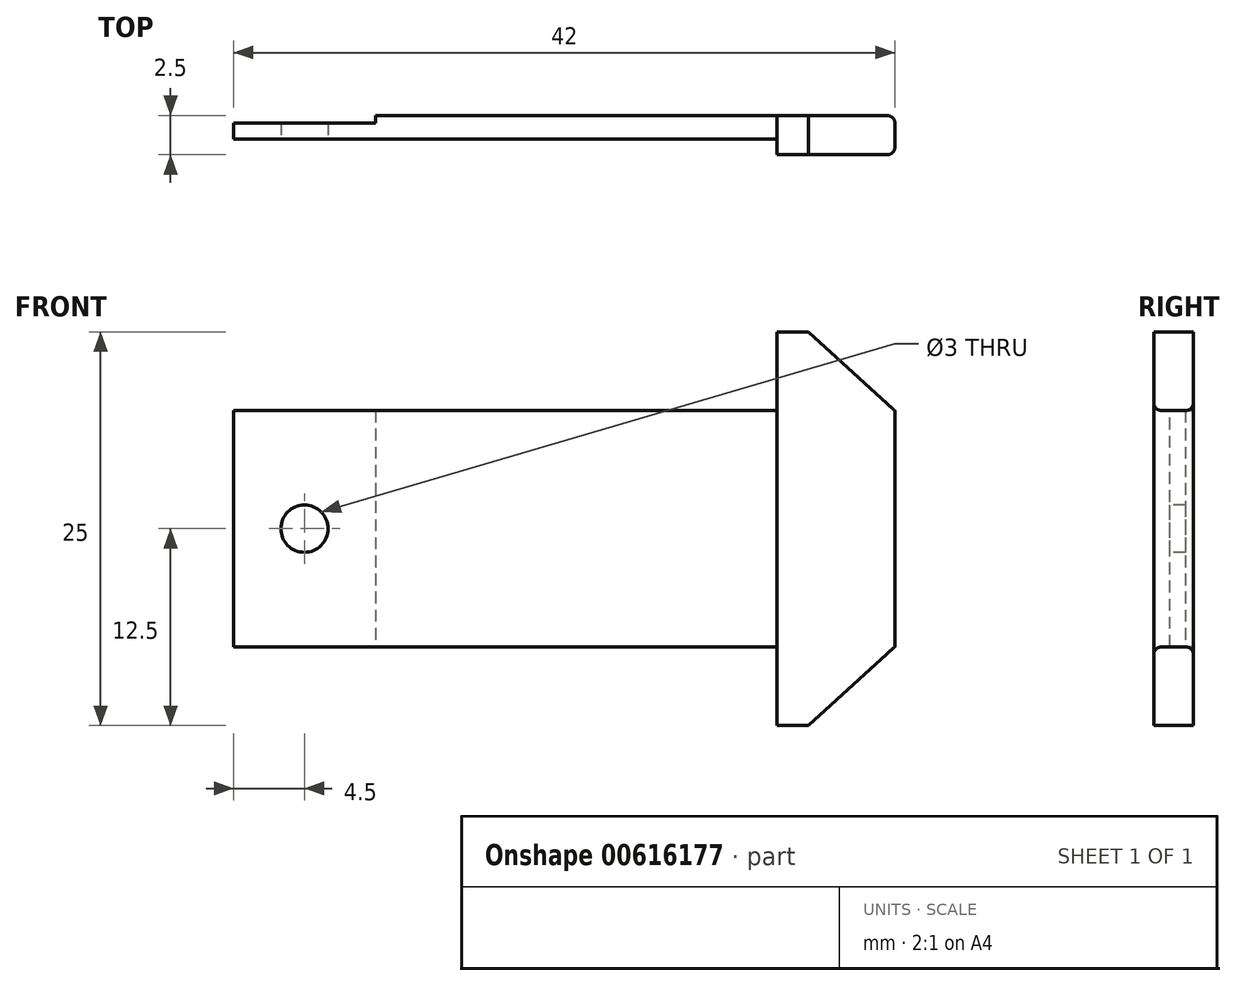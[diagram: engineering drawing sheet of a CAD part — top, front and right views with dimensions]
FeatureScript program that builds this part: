
annotation { "Feature Type Name" : "Feature", "Feature Type Description" : "" }
export const myFeature = defineFeature(function(context is Context, id is Id, definition is map)
    precondition{}
    {
        {
            var Q0;
            Q0=qCreatedBy(makeId("Front.planeOp"),FACE);
            var sketch = newSketch(context, id + "F0", { "sketchPlane" : qUnion([Q0])});
            skLineSegment(sketch, "E0.bottom", {"start": v(-17, 7.5) * mm, "end": v(25, 7.5) * mm});
            skLineSegment(sketch, "E0.top", {"start": v(-17, -7.5) * mm, "end": v(25, -7.5) * mm});
            skLineSegment(sketch, "E0.left", {"start": v(-17, 7.5) * mm, "end": v(-17, -7.5) * mm});
            skLineSegment(sketch, "E0.right", {"start": v(25, 7.5) * mm, "end": v(25, -7.5) * mm});
            skPoint(sketch, "E0.middle", {"position": v(4, 0) * mm});
            skSolve(sketch);
        }
        {
            var Q0;
            Q0=qSketchRegion(id+"F0",true);
            extrude(context, id + "F1", {"entities" : qUnion([Q0]), "depth" : 1.5 * mm, "offsetDistance" : 25 * mm});
        }
        {
            var Q0;
            Q0=makeQuery(id+"Fg7a1GXraSj58Eq_1.boolean.opBoolean","MERGE",FACE,{"derivedFrom":[makeQuery(id+"F1.opExtrude","CAP_FACE",FACE,{"disambiguationData":[OSD([sQuery(id+"F0.wireOp",EDGE,"E0.bottom"),sQuery(id+"F0.wireOp",EDGE,"E0.top"),sQuery(id+"F0.wireOp",EDGE,"E0.left"),sQuery(id+"F0.wireOp",EDGE,"E0.right")])],"isStart":false}),makeQuery(id+"Fg7a1GXraSj58Eq_1.opExtrude","CAP_FACE",FACE,{"disambiguationData":[OSD([sQuery(id+"F8gBCBH27mQZ7OE_1.wireOp",EDGE,"RbVLayld-Gt7w-auHQ-ZlfH-3jq96yst7m8C.bottom"),sQuery(id+"F8gBCBH27mQZ7OE_1.wireOp",EDGE,"RbVLayld-Gt7w-auHQ-ZlfH-3jq96yst7m8C.top"),sQuery(id+"F8gBCBH27mQZ7OE_1.wireOp",EDGE,"RbVLayld-Gt7w-auHQ-ZlfH-3jq96yst7m8C.left"),sQuery(id+"F8gBCBH27mQZ7OE_1.wireOp",EDGE,"RbVLayld-Gt7w-auHQ-ZlfH-3jq96yst7m8C.right")])],"isStart":true})]});
            var sketch = newSketch(context, id + "F2", { "sketchPlane" : qUnion([Q0])});
            skCircle(sketch, "E1", {"center": v(-12.5, 0) * mm, "radius": 1.5 * mm});
            skPoint(sketch, "E2", {"position": v(-17, 0) * mm});
            skSolve(sketch);
        }
        {
            var Q0;
            Q0 = qSketchRegion(id + "F2", true);
            extrude(context, id + "F3", {"entities" : qUnion([Q0]), "operationType" : NewBodyOperationType.REMOVE, "endBound" : BoundingType.THROUGH_ALL, "oppositeDirection" : true, "depth" : 25 * mm, "offsetDistance" : 25 * mm});
        }
        {
            var Q0;
            Q0=makeQuery(id+"F1.opExtrude","CAP_FACE",FACE,{"disambiguationData":[OSD([sQuery(id+"F0.wireOp",EDGE,"E0.bottom"),sQuery(id+"F0.wireOp",EDGE,"E0.top"),sQuery(id+"F0.wireOp",EDGE,"E0.left"),sQuery(id+"F0.wireOp",EDGE,"E0.right")])],"isStart":false});
            var sketch = newSketch(context, id + "F4", { "sketchPlane" : qUnion([Q0])});
            skLineSegment(sketch, "E3.bottom", {"start": v(25, -7.5) * mm, "end": v(17.5, -7.5) * mm});
            skLineSegment(sketch, "E3.top", {"start": v(19.5, -12.5) * mm, "end": v(17.5, -12.5) * mm});
            skLineSegment(sketch, "E3.right", {"start": v(17.5, -7.5) * mm, "end": v(17.5, -12.5) * mm});
            skLineSegment(sketch, "E4.bottom", {"start": v(25, 7.5) * mm, "end": v(17.5, 7.5) * mm});
            skLineSegment(sketch, "E4.top", {"start": v(19.5, 12.5) * mm, "end": v(17.5, 12.5) * mm});
            skLineSegment(sketch, "E4.right", {"start": v(17.5, 7.5) * mm, "end": v(17.5, 12.5) * mm});
            skLineSegment(sketch, "E5", {"start": v(17.5, -12.5) * mm, "end": v(19.5, -12.5) * mm});
            skLineSegment(sketch, "E6", {"start": v(19.5, -12.5) * mm, "end": v(25, -7.5) * mm});
            skLineSegment(sketch, "E7.MirrorCS", {"start": v(19.5, 12.5) * mm, "end": v(25, 7.5) * mm});
            skLineSegment(sketch, "E8.MirrorCS", {"start": v(17.5, 12.5) * mm, "end": v(19.5, 12.5) * mm});
            skSolve(sketch);
        }
        {
            var Q0;
            Q0 = qSketchRegion(id + "F4", true);
            var Q1;
            Q1=makeQuery(id+"F1.opExtrude","CAP_FACE",FACE,{"disambiguationData":[OSD([sQuery(id+"F0.wireOp",EDGE,"E0.bottom"),sQuery(id+"F0.wireOp",EDGE,"E0.top"),sQuery(id+"F0.wireOp",EDGE,"E0.left"),sQuery(id+"F0.wireOp",EDGE,"E0.right")])],"isStart":true});
            extrude(context, id + "F5", {"entities" : qUnion([Q0]), "operationType" : NewBodyOperationType.ADD, "endBound" : BoundingType.UP_TO_SURFACE, "oppositeDirection" : true, "depth" : 25 * mm, "endBoundEntityFace" : qUnion([Q1]), "offsetDistance" : 25 * mm});
        }
        {
            var Q0;
            Q0=makeQuery(id+"F1.opExtrude","SWEPT_FACE",FACE,{"disambiguationData":[OSD([sQuery(id+"F0.wireOp",EDGE,"E0.top")])]});
            var sketch = newSketch(context, id + "F6", { "sketchPlane" : qUnion([Q0])});
            skLineSegment(sketch, "E9.bottom", {"start": v(-17, 0) * mm, "end": v(-8, 0) * mm});
            skLineSegment(sketch, "E9.top", {"start": v(-17, 0.5) * mm, "end": v(-8, 0.5) * mm});
            skLineSegment(sketch, "E9.left", {"start": v(-17, 0) * mm, "end": v(-17, 0.5) * mm});
            skLineSegment(sketch, "E9.right", {"start": v(-8, 0) * mm, "end": v(-8, 0.5) * mm});
            skSolve(sketch);
        }
        {
            var Q0;
            Q0 = qSketchRegion(id + "F6", true);
            extrude(context, id + "F7", {"entities" : qUnion([Q0]), "operationType" : NewBodyOperationType.REMOVE, "endBound" : BoundingType.THROUGH_ALL, "oppositeDirection" : true, "depth" : 25 * mm, "offsetDistance" : 25 * mm});
        }
        {
            var Q0;
            Q0=makeQuery(id+"F5.boolean.opBoolean","MERGE",FACE,{"derivedFrom":[makeQuery(id+"F1.opExtrude","CAP_FACE",FACE,{"disambiguationData":[OSD([sQuery(id+"F0.wireOp",EDGE,"E0.bottom"),sQuery(id+"F0.wireOp",EDGE,"E0.top"),sQuery(id+"F0.wireOp",EDGE,"E0.left"),sQuery(id+"F0.wireOp",EDGE,"E0.right")])],"isStart":false}),makeQuery(id+"F5.opExtrude","CAP_FACE",FACE,{"disambiguationData":[OSD([sQuery(id+"F4.wireOp",EDGE,"E3.bottom"),sQuery(id+"F4.wireOp",EDGE,"E3.right"),sQuery(id+"F4.wireOp",EDGE,"E5"),sQuery(id+"F4.wireOp",EDGE,"E6")])],"isStart":true}),makeQuery(id+"F5.opExtrude","CAP_FACE",FACE,{"disambiguationData":[OSD([sQuery(id+"F4.wireOp",EDGE,"E4.bottom"),sQuery(id+"F4.wireOp",EDGE,"E4.right"),sQuery(id+"F4.wireOp",EDGE,"E7.MirrorCS"),sQuery(id+"F4.wireOp",EDGE,"E8.MirrorCS")])],"isStart":true})]});
            var sketch = newSketch(context, id + "F8", { "sketchPlane" : qUnion([Q0])});
            skLineSegment(sketch, "E10.0", {"start": v(19.5, 12.5) * mm, "end": v(25, 7.5) * mm});
            skLineSegment(sketch, "E11.0", {"start": v(25, 7.5) * mm, "end": v(25, -7.5) * mm});
            skLineSegment(sketch, "E12.0", {"start": v(19.5, -12.5) * mm, "end": v(25, -7.5) * mm});
            skLineSegment(sketch, "E13", {"start": v(19.5, 12.5) * mm, "end": v(17.5, 12.5) * mm});
            skLineSegment(sketch, "E14", {"start": v(17.5, 12.5) * mm, "end": v(17.5, -12.5) * mm});
            skLineSegment(sketch, "E15", {"start": v(17.5, -12.5) * mm, "end": v(19.5, -12.5) * mm});
            skSolve(sketch);
        }
        {
            var Q0;
            Q0 = qSketchRegion(id + "F8", true);
            extrude(context, id + "F9", {"entities" : qUnion([Q0]), "operationType" : NewBodyOperationType.ADD, "depth" : 1 * mm, "offsetDistance" : 25 * mm});
        }
        {
            var Q0;
            Q0=makeQuery(id+"F9.opExtrude","CAP_EDGE",EDGE,{"disambiguationData":[OSD([sQuery(id+"F8.wireOp",EDGE,"E11.0")])],"isStart":false});
            var Q1;
            Q1=makeQuery(id+"F1.opExtrude","CAP_EDGE",EDGE,{"disambiguationData":[OSD([sQuery(id+"F0.wireOp",EDGE,"E0.right")])],"isStart":true});
            fillet(context, id + "F10", {"entities" : qUnion([Q0, Q1]), "radius" : 0.5 * mm, "tangentPropagation" : true, "allowEdgeOverflow" : false});
        }
    });
